# Revit family: Qf_Summit_AIWD282_Countertop_Ice_and_Water_Dispenser
name_source: partatom
category: Specialty Equipment
units: mm (PartAtom-declared; Revit-internal decimal feet)

## family parameters
Always vertical = Yes
Cut with Voids When Loaded = No
Part Type = Normal
Room Calculation Point = No
Round Connector Dimension = Use Diameter
Shared = No
Work Plane-Based = No

## types (1)
- Qf_Summit_AIWD282_Countertop_Ice_and_Water_Dispenser
    Apparent Power = 667 VA
    Cold Water Connection Height = 0"
    Cold Water Flow = 0 GPM
    Cold Water Maximum Pressure = 0.00 psi
    Cold Water Minimum Pressure = 0.00 psi
    Cold Water RI Height = 0"
    Cold Water Size = 0"
    Cold Water Temperature Recommended = -460 °F
    Conn Conduit = Yes
    Cycle = 60 Hz
    Default Elevation = 0"
    Depth = 25"
    Description = Countertop Ice and Water Dispenser
    Direct Waste Connection Height = 0"
    Direct Waste Flow = 0 GPM
    Direct Waste RI Height = 0"
    Direct Waste Size = 1"
    Elec Conn Connection Height = 0"
    Elec Conn RI Height = 0"
    FL Amps = 6 A
    Foodservice Equipment Identifier = Yes
    Height = 31 1/4"
    Identify Quantity as Lot = Yes
    Indirect Waste Connection Height = 0"
    Indirect Waste Flow = 0 GPM
    Indirect Waste Size = 0"
    Length = 16 1/2"
    Manufacturer = Summit
    Max Overcurrent Protection = 0 A
    Min Ckt Ampacity = 0 A
    Model = AIWD282
    Number of Poles = 1
    Phase = 1
    Refrigerant Type = R404a
    URL = www.summitappliance.com
    URL Cutsheet = www.summitappliance.com
    Volts = 115 V
    Waste Water Discharge Temperature = -460 °F
    Watts = 667 W
    Weight in Pounds = 146

## geometry (parser evidence)
native form markers: Blend x4, Sweep x1
no freeform markers — native parametric forms only
